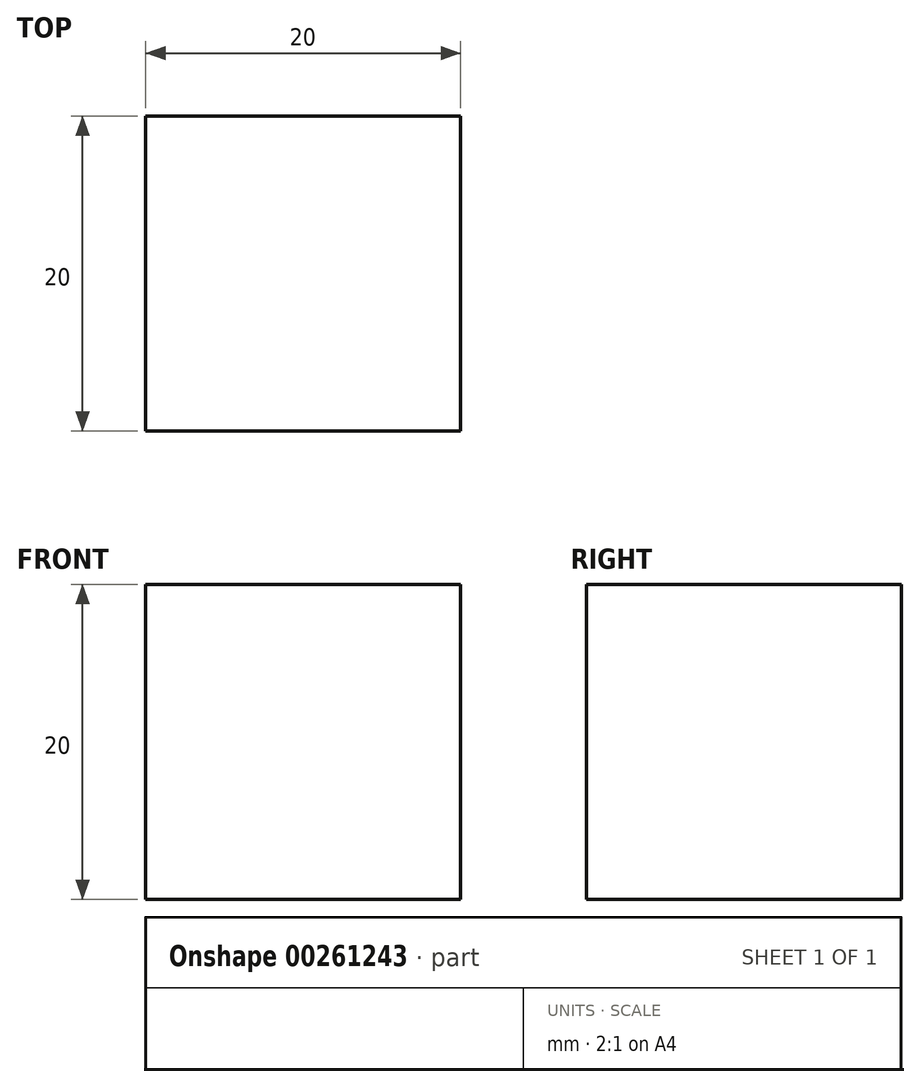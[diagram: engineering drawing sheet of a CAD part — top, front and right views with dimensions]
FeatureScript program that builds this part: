
annotation { "Feature Type Name" : "Feature", "Feature Type Description" : "" }
export const myFeature = defineFeature(function(context is Context, id is Id, definition is map)
    precondition{}
    {
        {
            var Q0;
            Q0=qCreatedBy(makeId("Front.planeOp"),FACE);
            var sketch = newSketch(context, id + "F0", { "sketchPlane" : qUnion([Q0])});
            skLineSegment(sketch, "E0.bottom", {"start": v(-2.6, 11.8) * mm, "end": v(17.4, 11.8) * mm});
            skLineSegment(sketch, "E0.top", {"start": v(-2.6, -8.2) * mm, "end": v(17.4, -8.2) * mm});
            skLineSegment(sketch, "E0.left", {"start": v(-2.6, 11.8) * mm, "end": v(-2.6, -8.2) * mm});
            skLineSegment(sketch, "E0.right", {"start": v(17.4, 11.8) * mm, "end": v(17.4, -8.2) * mm});
            skSolve(sketch);
        }
        {
            var Q0;
            Q0=makeQuery(id+"F0.imprint","IMPRINT",FACE,{"disambiguationData":[TD([[makeQuery(id+"F0.imprint","IMPRINT",EDGE,{"derivedFrom":sQuery(id+"F0.wireOp",EDGE,"E0.bottom")}),-1.0]])]});
            extrude(context, id + "F1", {"entities" : qUnion([Q0]), "depth" : 20 * mm});
        }
    });
